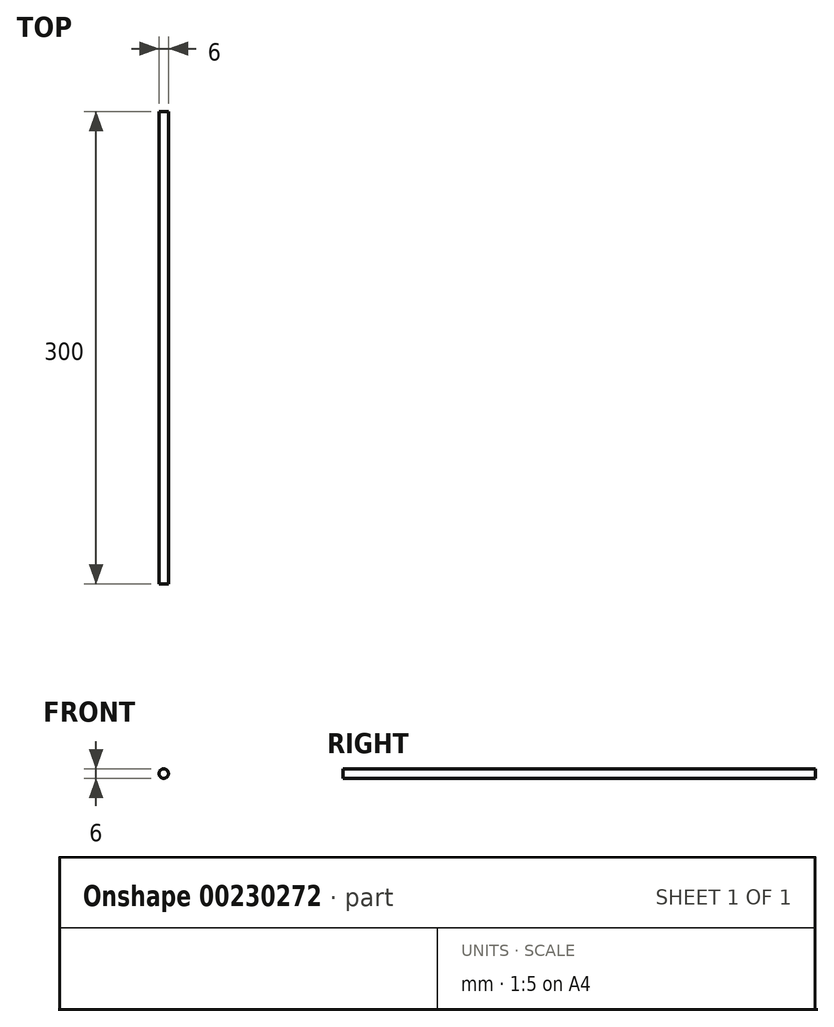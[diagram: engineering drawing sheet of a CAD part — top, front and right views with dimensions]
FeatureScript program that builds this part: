
annotation { "Feature Type Name" : "Feature", "Feature Type Description" : "" }
export const myFeature = defineFeature(function(context is Context, id is Id, definition is map)
    precondition{}
    {
        {
            var Q0;
            Q0=qCreatedBy(makeId("Front.planeOp"),FACE);
            var sketch = newSketch(context, id + "F0", { "sketchPlane" : qUnion([Q0])});
            skCircle(sketch, "E0", {"center": v(0, 0) * mm, "radius": 3 * mm});
            skSolve(sketch);
        }
        {
            var Q0;
            Q0=makeQuery(id+"F0.imprint","IMPRINT",FACE,{"disambiguationData":[TD([[makeQuery(id+"F0.imprint","IMPRINT",EDGE,{"derivedFrom":sQuery(id+"F0.wireOp",EDGE,"E0")}),1.0]])]});
            extrude(context, id + "F1", {"entities" : qUnion([Q0]), "endBound" : BoundingType.SYMMETRIC, "depth" : 300 * mm});
        }
    });
